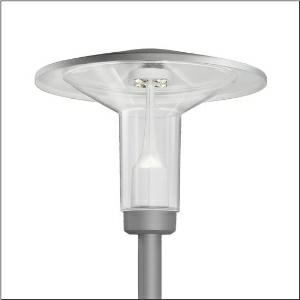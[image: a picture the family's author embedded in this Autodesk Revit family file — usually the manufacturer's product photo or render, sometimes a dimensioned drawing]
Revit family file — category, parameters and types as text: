
# Revit family: laterne___p1_0a_5xa5255ff14h_e703
name_source: partatom
category: Lighting Fixtures
units: mm (PartAtom-declared; Revit-internal decimal feet)

## family parameters
Cut with Voids When Loaded = No
Host = Face
Light Source = No
Part Type = Normal
Room Calculation Point = No
Round Connector Dimension = Use Diameter
Shared = No

## types (1)
- --- (1 x LED, 1510 lm, 10.5 W, 3000K)
    Apparent Load = 11 VA
    CIE Flux Codes = 35 64 91 96 100
    Color Rendering = 70
    Color Temperature = 3000K
    Default Elevation = 1800 mm
    Description = Lantern, mast luminaire, Module 540 iQ-SR, primary light control with 3 zone facetted reflector, of plastic, silver coated, highly specular, structured, primary optical cover: cover, of PMMA, transparent, light distribution: P1.0a, light emission: direct distribution, primary light characteristic: strongly asymmetric, installation type: post-top, LED, High Power LED, rated luminous flux: 1.510lm, luminous efficacy: 144lm/W, light colour: 730, colour temperature: 3000K, control gear: ECG iQ, control: Auto-Match, Temp-Guard, Lumen-Switch, Night-Set, Smart-Wire, Light-Fading, Desk-Remote (wireless, voltage-free reading and setting of iQ features in the workshop via application-optimized NFC function/RFID function), optimised constant luminous flux control (CLO 2.0), Street-Remote, presetting dimming logarithmic, with terminal, 6-pole, max. 2.5mm², mains connection: 220..240V, AC, 50/60Hz, start of lifetime: 11W, end of lifetime: 11W, reduction: 5W, luminaire housing, upper part, of glass-fibre reinforced polyester, coated, Siteco® metallic grey (DB 702S), diameter: 750mm, height: 583mm, spigot size: d x l = 76 x 70mm (post-top) | with reducer (optional accessory) 60 x 70mm, post-top mast mounting element, of diecast aluminium, coated, Siteco® metallic grey (DB 702S), Module 540 iQ-SR, traffic white (RAL 9016), equipment: standard, protection rating (complete): IP65, insulation class (complete): insulation class II (safety insulation), certification: CE, ENEC, VDE, packaging unit: 1 piece

Light Distribution: P1.0a
    Height = 583 mm
    Lamp = 1 x LED
    Lamp Light Flux = 1510 lm
    Lamp Power = 10.5 W
    Lamp count = 1
    Length = 750 mm
    Luminous efficacy = 144 lm/W
    Manufacturer = Siteco
    ModVariant = No
    Model = 5XA5255FF14H
    Number of Poles = 1
    OnlyDefault = Yes
    Power Factor = 1
    Product Name = Laterne | P1.0a
    Product group = mast luminaire | pylon top
    ProductGroupID = 6100
    Protection Class = Protection class II
    Protection Degree = IP 65
    RLX_Detail_Level = 1
    RlxData = <blob elided: 74053 chars, md5=ff7894af>
    Socket = socket
    Standby Power = 0 W
    System Light Flux = 1510 lm
    System Power = 11 W
    Type Comments = factory setting: luminous flux: 100 % | dim-lin: 254 | 419 mA
    Type Image = l_1006050.jpg
    URL = http://relux.com
    VarID = @adj_071751
    Voltage = 0 V
    Weight = 0.00 kg
    Width = 0 mm  [stored 0 ft]

note: [stored X ft] marks values corroborated as IEEE doubles in the binary element streams (Revit-internal decimal feet)

## geometry (parser evidence)
native form markers: Blend x4, Sweep x11
no freeform markers — native parametric forms only
